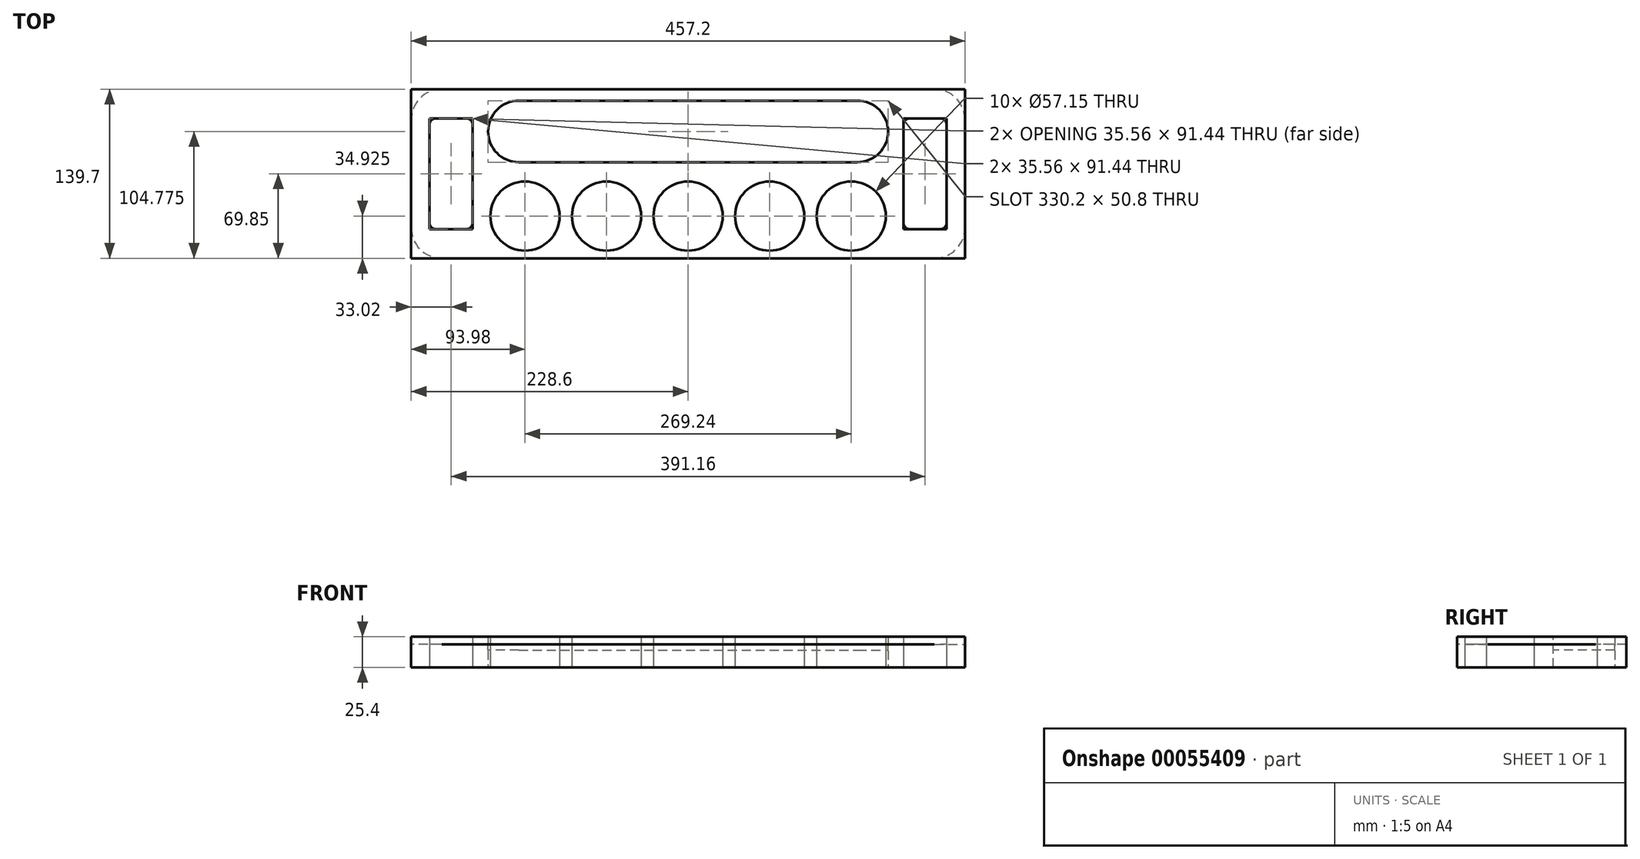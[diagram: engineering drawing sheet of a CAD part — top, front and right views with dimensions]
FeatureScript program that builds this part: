
annotation { "Feature Type Name" : "Feature", "Feature Type Description" : "" }
export const myFeature = defineFeature(function(context is Context, id is Id, definition is map)
    precondition{}
    {
        {
            var Q0;
            Q0=qCreatedBy(makeId("Top.planeOp"),FACE);
            var sketch = newSketch(context, id + "F0", { "sketchPlane" : qUnion([Q0])});
            skLineSegment(sketch, "E0", {"start": v(-228.6, 69.85) * mm, "end": v(228.6, 69.85) * mm});
            skLineSegment(sketch, "E1", {"start": v(-228.6, -69.85) * mm, "end": v(-228.6, 69.85) * mm});
            skLineSegment(sketch, "E2", {"start": v(228.6, 69.85) * mm, "end": v(228.6, -69.85) * mm});
            skLineSegment(sketch, "E3", {"start": v(228.6, -69.85) * mm, "end": v(-228.6, -69.85) * mm});
            skCircle(sketch, "E4", {"center": v(-134.62, -34.92) * mm, "radius": 28.58 * mm});
            skCircle(sketch, "E5", {"center": v(-67.31, -34.92) * mm, "radius": 28.58 * mm});
            skCircle(sketch, "E6", {"center": v(0, -34.92) * mm, "radius": 28.58 * mm});
            skLineSegment(sketch, "E7", {"start": v(213.36, 45.72) * mm, "end": v(177.8, 45.72) * mm});
            skLineSegment(sketch, "E8", {"start": v(177.8, 45.72) * mm, "end": v(177.8, -45.72) * mm});
            skLineSegment(sketch, "E9", {"start": v(177.8, -45.72) * mm, "end": v(213.36, -45.72) * mm});
            skLineSegment(sketch, "E10", {"start": v(213.36, -45.72) * mm, "end": v(213.36, 45.72) * mm});
            skCircle(sketch, "E11", {"center": v(134.62, -34.92) * mm, "radius": 28.58 * mm});
            skArc(sketch, "E12", {"start": v(139.7, 9.53) * mm, "mid": v(165.1, 34.93) * mm, "end": v(139.7, 60.32) * mm});
            skLineSegment(sketch, "E13", {"start": v(-139.7, 9.53) * mm, "end": v(139.7, 9.53) * mm});
            skLineSegment(sketch, "E14", {"start": v(-139.7, 60.33) * mm, "end": v(139.7, 60.33) * mm});
            skArc(sketch, "E15", {"start": v(-139.7, 60.32) * mm, "mid": v(-165.1, 34.93) * mm, "end": v(-139.7, 9.53) * mm});
            skCircle(sketch, "E16", {"center": v(67.31, -34.92) * mm, "radius": 28.58 * mm});
            skLineSegment(sketch, "E17", {"start": v(-213.36, 45.72) * mm, "end": v(-177.8, 45.72) * mm});
            skLineSegment(sketch, "E18", {"start": v(-213.36, -45.72) * mm, "end": v(-213.36, 45.72) * mm});
            skLineSegment(sketch, "E19", {"start": v(-177.8, 45.72) * mm, "end": v(-177.8, -45.72) * mm});
            skLineSegment(sketch, "E20", {"start": v(-177.8, -45.72) * mm, "end": v(-213.36, -45.72) * mm});
            skSolve(sketch);
        }
        {
            var Q0;
            Q0=qSketchRegion(id+"F0",true);
            extrude(context, id + "F1", {"entities" : qUnion([Q0]), "depth" : 25.4 * mm});
        }
        {
            var Q0;
            Q0=qCreatedBy(makeId("Top.planeOp"),FACE);
            var sketch = newSketch(context, id + "F2", { "sketchPlane" : qUnion([Q0])});
            skLineSegment(sketch, "E21.rect.bottom", {"start": v(228.6, 69.85) * mm, "end": v(-228.6, 69.85) * mm});
            skLineSegment(sketch, "E21.rect.top", {"start": v(228.6, -69.85) * mm, "end": v(-228.6, -69.85) * mm});
            skLineSegment(sketch, "E21.rect.left", {"start": v(228.6, 69.85) * mm, "end": v(228.6, -69.85) * mm});
            skLineSegment(sketch, "E21.rect.right", {"start": v(-228.6, 69.85) * mm, "end": v(-228.6, -69.85) * mm});
            skPoint(sketch, "E21.rect.middle", {"position": v(0, 0) * mm});
            skCircle(sketch, "E22", {"center": v(-134.62, -34.93) * mm, "radius": 28.58 * mm});
            skCircle(sketch, "E23", {"center": v(-67.31, -34.93) * mm, "radius": 28.58 * mm});
            skCircle(sketch, "E24", {"center": v(0, -34.93) * mm, "radius": 28.58 * mm});
            skCircle(sketch, "E25", {"center": v(67.31, -34.92) * mm, "radius": 28.58 * mm});
            skCircle(sketch, "E26", {"center": v(134.62, -34.92) * mm, "radius": 28.58 * mm});
            skLineSegment(sketch, "E27.rect.bottom", {"start": v(-182.88, -45.72) * mm, "end": v(-208.28, -45.72) * mm});
            skLineSegment(sketch, "E27.rect.top", {"start": v(-182.88, 45.72) * mm, "end": v(-208.28, 45.72) * mm});
            skLineSegment(sketch, "E27.rect.left", {"start": v(-177.8, -40.64) * mm, "end": v(-177.8, 40.64) * mm});
            skLineSegment(sketch, "E27.rect.right", {"start": v(-213.36, -40.64) * mm, "end": v(-213.36, 40.64) * mm});
            skPoint(sketch, "E27.rect.middle", {"position": v(-195.58, 0) * mm});
            skLineSegment(sketch, "E28.MirrorCS", {"start": v(177.8, -40.64) * mm, "end": v(177.8, 40.64) * mm});
            skLineSegment(sketch, "E29.MirrorCS", {"start": v(182.88, -45.72) * mm, "end": v(208.28, -45.72) * mm});
            skLineSegment(sketch, "E30.MirrorCS", {"start": v(182.88, 45.72) * mm, "end": v(208.28, 45.72) * mm});
            skLineSegment(sketch, "E31.MirrorCS", {"start": v(213.36, -40.64) * mm, "end": v(213.36, 40.64) * mm});
            skPoint(sketch, "E32.visualSharp", {"position": v(-177.8, 45.72) * mm});
            skArc(sketch, "E32.filletArc", {"start": v(-177.8, 40.64) * mm, "mid": v(-179.29, 44.23) * mm, "end": v(-182.88, 45.72) * mm});
            skPoint(sketch, "E33.visualSharp", {"position": v(-213.36, 45.72) * mm});
            skArc(sketch, "E33.filletArc", {"start": v(-208.28, 45.72) * mm, "mid": v(-211.87, 44.23) * mm, "end": v(-213.36, 40.64) * mm});
            skPoint(sketch, "E34.visualSharp", {"position": v(-213.36, -45.72) * mm});
            skArc(sketch, "E34.filletArc", {"start": v(-213.36, -40.64) * mm, "mid": v(-211.87, -44.23) * mm, "end": v(-208.28, -45.72) * mm});
            skPoint(sketch, "E35.visualSharp", {"position": v(-177.8, -45.72) * mm});
            skArc(sketch, "E35.filletArc", {"start": v(-182.88, -45.72) * mm, "mid": v(-179.29, -44.23) * mm, "end": v(-177.8, -40.64) * mm});
            skPoint(sketch, "E36.visualSharp", {"position": v(213.36, 45.72) * mm});
            skArc(sketch, "E36.filletArc", {"start": v(213.36, 40.64) * mm, "mid": v(211.87, 44.23) * mm, "end": v(208.28, 45.72) * mm});
            skPoint(sketch, "E37.visualSharp", {"position": v(177.8, 45.72) * mm});
            skArc(sketch, "E37.filletArc", {"start": v(182.88, 45.72) * mm, "mid": v(179.29, 44.23) * mm, "end": v(177.8, 40.64) * mm});
            skPoint(sketch, "E38.visualSharp", {"position": v(177.8, -45.72) * mm});
            skArc(sketch, "E38.filletArc", {"start": v(177.8, -40.64) * mm, "mid": v(179.29, -44.23) * mm, "end": v(182.88, -45.72) * mm});
            skPoint(sketch, "E39.visualSharp", {"position": v(213.36, -45.72) * mm});
            skArc(sketch, "E39.filletArc", {"start": v(208.28, -45.72) * mm, "mid": v(211.87, -44.23) * mm, "end": v(213.36, -40.64) * mm});
            skSolve(sketch);
        }
        {
            var Q0;
            Q0=qSketchRegion(id+"F2",true);
            extrude(context, id + "F3", {"entities" : qUnion([Q0]), "depth" : 19.05 * mm});
        }
        {
            var Q0;
            Q0=makeQuery(id+"F3.opExtrude","CAP_FACE",FACE,{"disambiguationData":[OSD([sQuery(id+"F2.wireOp",EDGE,"E21.rect.bottom"),sQuery(id+"F2.wireOp",EDGE,"E21.rect.top"),sQuery(id+"F2.wireOp",EDGE,"E21.rect.left"),sQuery(id+"F2.wireOp",EDGE,"E21.rect.right"),sQuery(id+"F2.wireOp",EDGE,"E22"),sQuery(id+"F2.wireOp",EDGE,"E23"),sQuery(id+"F2.wireOp",EDGE,"E24"),sQuery(id+"F2.wireOp",EDGE,"E25"),sQuery(id+"F2.wireOp",EDGE,"E26"),sQuery(id+"F2.wireOp",EDGE,"E27.rect.bottom"),sQuery(id+"F2.wireOp",EDGE,"E27.rect.top"),sQuery(id+"F2.wireOp",EDGE,"E27.rect.left"),sQuery(id+"F2.wireOp",EDGE,"E27.rect.right"),sQuery(id+"F2.wireOp",EDGE,"E28.MirrorCS"),sQuery(id+"F2.wireOp",EDGE,"E29.MirrorCS"),sQuery(id+"F2.wireOp",EDGE,"E30.MirrorCS"),sQuery(id+"F2.wireOp",EDGE,"E31.MirrorCS")])],"isStart":false});
            var sketch = newSketch(context, id + "F4", { "sketchPlane" : qUnion([Q0])});
            skLineSegment(sketch, "E40", {"start": v(0, 66.83) * mm, "end": v(0, 22.79) * mm, "construction": true});
            skLineSegment(sketch, "E41", {"start": v(-139.7, 34.92) * mm, "end": v(139.7, 34.93) * mm, "construction": true});
            skArc(sketch, "E42.0.startCap", {"start": v(-139.7, 9.53) * mm, "mid": v(-165.1, 34.93) * mm, "end": v(-139.7, 60.33) * mm});
            skArc(sketch, "E42.0.endCap", {"start": v(139.7, 60.33) * mm, "mid": v(165.1, 34.93) * mm, "end": v(139.7, 9.53) * mm});
            skLineSegment(sketch, "E42.0.left", {"start": v(-139.7, 60.33) * mm, "end": v(139.7, 60.33) * mm});
            skLineSegment(sketch, "E42.0.right", {"start": v(-139.7, 9.53) * mm, "end": v(139.7, 9.53) * mm});
            skSolve(sketch);
        }
        {
            var Q0;
            Q0=qSketchRegion(id+"F4",true);
            extrude(context, id + "F5", {"entities" : qUnion([Q0]), "operationType" : NewBodyOperationType.REMOVE, "oppositeDirection" : true, "depth" : 4.76 * mm});
        }
        {
            var Q0;
            Q0=makeQuery(id+"F3.opExtrude","SWEPT_EDGE",EDGE,{"disambiguationData":[OSD([sQuery(id+"F2.wireOp",EDGE,"E21.rect.top"),sQuery(id+"F2.wireOp",EDGE,"E21.rect.left")])]});
            var Q1;
            Q1=makeQuery(id+"F3.opExtrude","SWEPT_EDGE",EDGE,{"disambiguationData":[OSD([sQuery(id+"F2.wireOp",EDGE,"E21.rect.bottom"),sQuery(id+"F2.wireOp",EDGE,"E21.rect.left")])]});
            var Q2;
            Q2=makeQuery(id+"F3.opExtrude","SWEPT_EDGE",EDGE,{"disambiguationData":[OSD([sQuery(id+"F2.wireOp",EDGE,"E21.rect.top"),sQuery(id+"F2.wireOp",EDGE,"E21.rect.right")])]});
            var Q3;
            Q3=makeQuery(id+"F3.opExtrude","SWEPT_EDGE",EDGE,{"disambiguationData":[OSD([sQuery(id+"F2.wireOp",EDGE,"E21.rect.bottom"),sQuery(id+"F2.wireOp",EDGE,"E21.rect.right")])]});
            fillet(context, id + "F6", {"entities" : qUnion([Q0, Q1, Q2, Q3]), "radius" : 25.4 * mm, "tangentPropagation" : true, "allowEdgeOverflow" : false});
        }
    });
